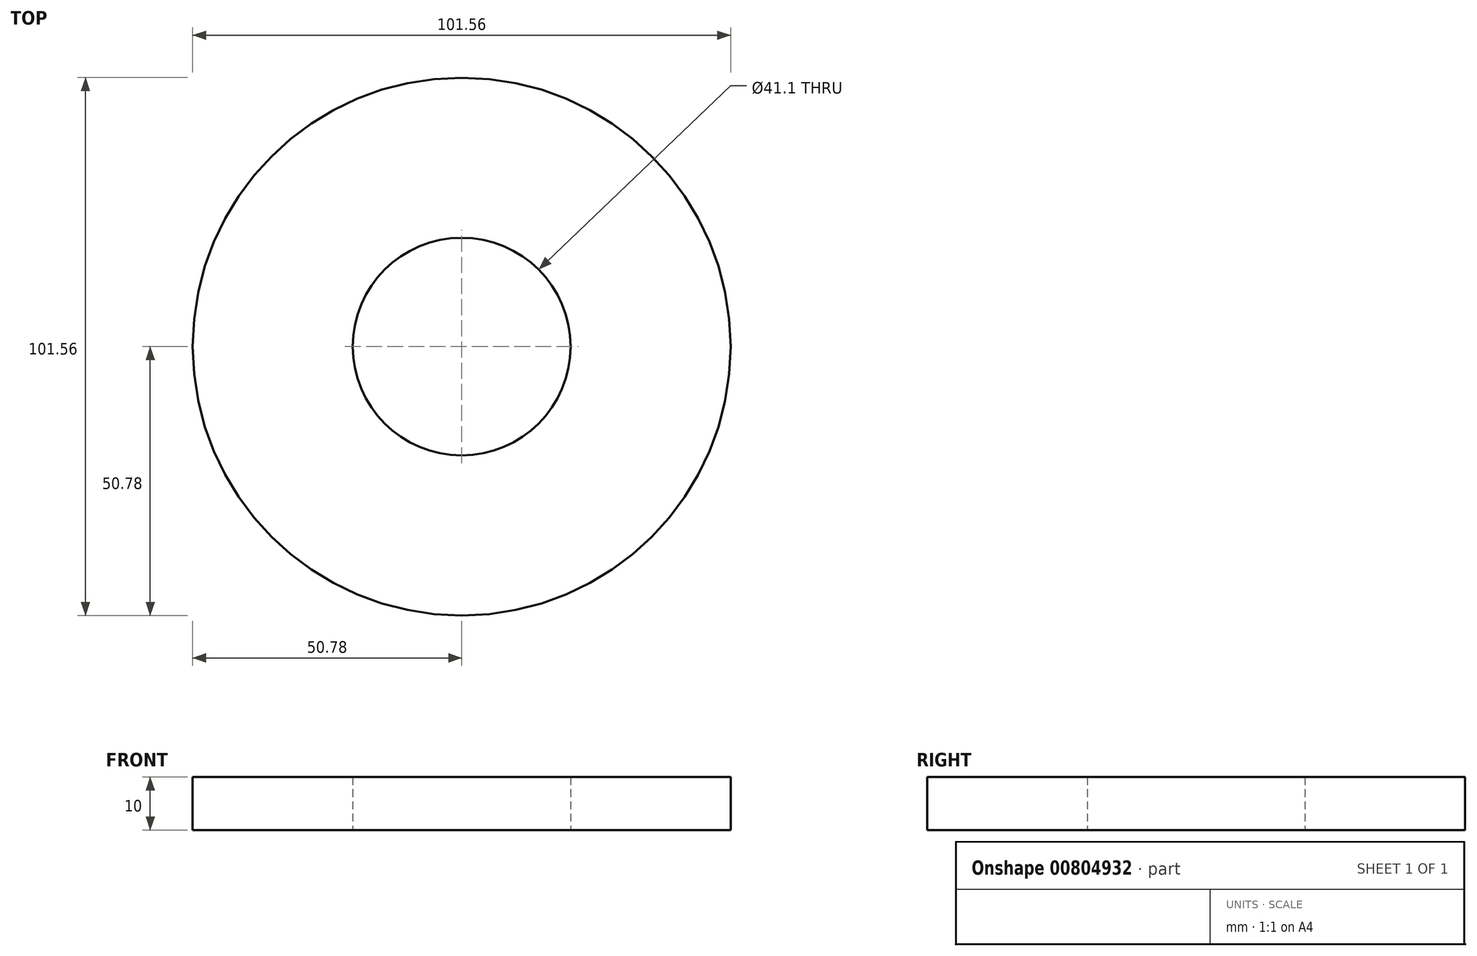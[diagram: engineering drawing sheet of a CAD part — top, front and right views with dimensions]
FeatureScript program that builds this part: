
annotation { "Feature Type Name" : "Feature", "Feature Type Description" : "" }
export const myFeature = defineFeature(function(context is Context, id is Id, definition is map)
    precondition{}
    {
        {
            var Q0;
            Q0=qCreatedBy(makeId("Top.planeOp"),FACE);
            var sketch = newSketch(context, id + "F0", { "sketchPlane" : qUnion([Q0])});
            skCircle(sketch, "E0", {"center": v(0, 0) * mm, "radius": 20.55 * mm});
            skCircle(sketch, "E1", {"center": v(0, 0) * mm, "radius": 50.77 * mm});
            skSolve(sketch);
        }
        {
            var Q0;
            Q0 = qSketchRegion(id + "F0", true);
            extrude(context, id + "F1", {"entities" : qUnion([Q0]), "depth" : 10 * mm, "offsetDistance" : 25 * mm});
        }
    });
